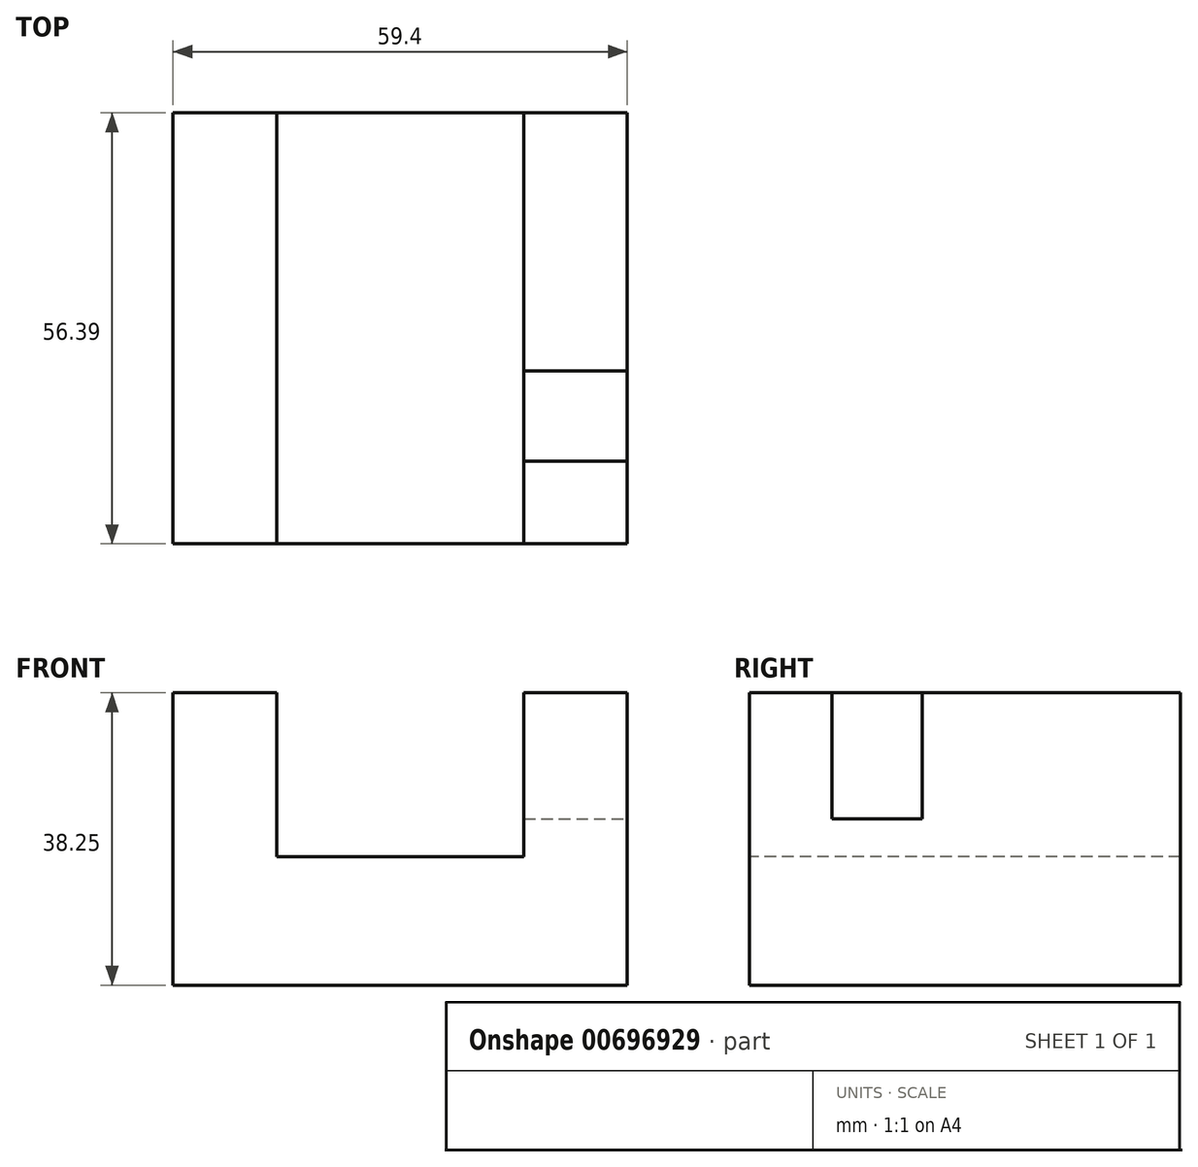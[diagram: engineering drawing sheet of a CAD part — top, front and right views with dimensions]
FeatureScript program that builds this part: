
annotation { "Feature Type Name" : "Feature", "Feature Type Description" : "" }
export const myFeature = defineFeature(function(context is Context, id is Id, definition is map)
    precondition{}
    {
        {
            var Q0;
            Q0=qCreatedBy(makeId("Front.planeOp"),FACE);
            var sketch = newSketch(context, id + "F0", { "sketchPlane" : qUnion([Q0])});
            skLineSegment(sketch, "E0.bottom", {"start": v(0, 0) * mm, "end": v(59.4, 0) * mm});
            skLineSegment(sketch, "E0.top", {"start": v(0, 38.25) * mm, "end": v(13.53, 38.25) * mm});
            skLineSegment(sketch, "E0.left", {"start": v(0, 0) * mm, "end": v(0, 38.25) * mm});
            skLineSegment(sketch, "E0.right", {"start": v(59.4, 0) * mm, "end": v(59.4, 38.25) * mm});
            skLineSegment(sketch, "E1.top", {"start": v(45.87, 16.8) * mm, "end": v(13.53, 16.8) * mm});
            skLineSegment(sketch, "E1.left", {"start": v(45.87, 38.25) * mm, "end": v(45.87, 16.8) * mm});
            skLineSegment(sketch, "E1.right", {"start": v(13.53, 38.25) * mm, "end": v(13.53, 16.8) * mm});
            skLineSegment(sketch, "E2.trimOffspring", {"start": v(45.87, 38.25) * mm, "end": v(59.4, 38.25) * mm});
            skSolve(sketch);
        }
        {
            var Q0;
            Q0=makeQuery(id+"F0.imprint","IMPRINT",FACE,{"disambiguationData":[TD([[makeQuery(id+"F0.imprint","IMPRINT",EDGE,{"derivedFrom":sQuery(id+"F0.wireOp",EDGE,"E0.bottom")}),1.0]])]});
            extrude(context, id + "F1", {"entities" : qUnion([Q0]), "oppositeDirection" : true, "depth" : 56.4 * mm, "offsetDistance" : 25.4 * mm});
        }
        {
            var Q0;
            Q0=makeQuery(id+"F1.opExtrude","SWEPT_FACE",FACE,{"disambiguationData":[OSD([sQuery(id+"F0.wireOp",EDGE,"E2.trimOffspring")])]});
            var sketch = newSketch(context, id + "F2", { "sketchPlane" : qUnion([Q0])});
            skLineSegment(sketch, "E3.bottom", {"start": v(45.87, 10.78) * mm, "end": v(59.4, 10.78) * mm});
            skLineSegment(sketch, "E3.top", {"start": v(45.87, 22.6) * mm, "end": v(59.4, 22.6) * mm});
            skLineSegment(sketch, "E3.left", {"start": v(45.87, 10.78) * mm, "end": v(45.87, 22.6) * mm});
            skLineSegment(sketch, "E3.right", {"start": v(59.4, 10.78) * mm, "end": v(59.4, 22.6) * mm});
            skSolve(sketch);
        }
        {
            var Q0;
            Q0=makeQuery(id+"F2.imprint","IMPRINT",FACE,{"disambiguationData":[TD([[makeQuery(id+"F2.imprint","IMPRINT",EDGE,{"derivedFrom":sQuery(id+"F2.wireOp",EDGE,"E3.bottom")}),1.0]])]});
            extrude(context, id + "F3", {"entities" : qUnion([Q0]), "operationType" : NewBodyOperationType.REMOVE, "oppositeDirection" : true, "depth" : 16.5 * mm, "offsetDistance" : 25.4 * mm});
        }
    });
